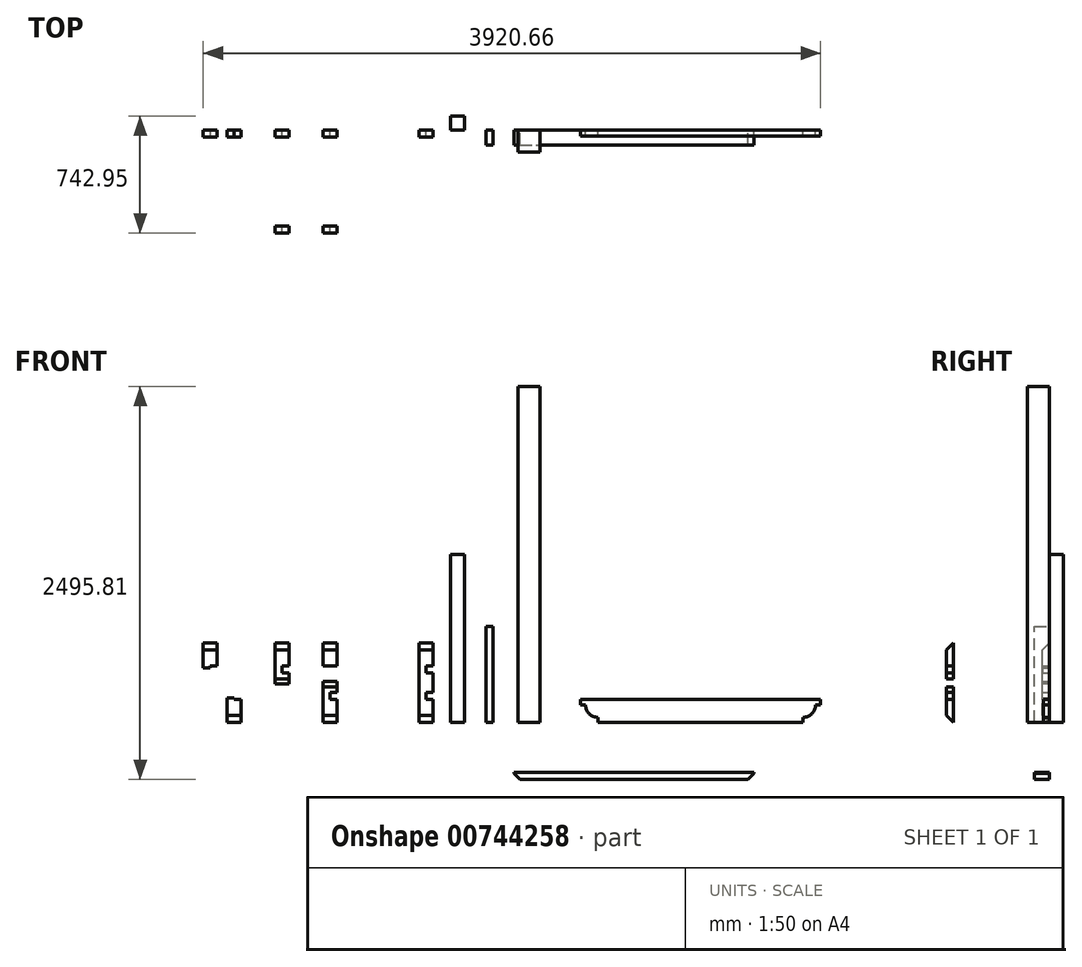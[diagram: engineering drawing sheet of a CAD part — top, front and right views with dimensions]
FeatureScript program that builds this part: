
annotation { "Feature Type Name" : "Feature", "Feature Type Description" : "" }
export const myFeature = defineFeature(function(context is Context, id is Id, definition is map)
    precondition{}
    {
        {
            var Q0;
            Q0=qCreatedBy(makeId("Front.planeOp"),FACE);
            var sketch = newSketch(context, id + "F0", { "sketchPlane" : qUnion([Q0])});
            skLineSegment(sketch, "E0.bottom", {"start": v(25.4, 0) * mm, "end": v(165.1, 0) * mm});
            skLineSegment(sketch, "E0.top", {"start": v(25.4, 2133.6) * mm, "end": v(165.1, 2133.6) * mm});
            skLineSegment(sketch, "E0.left", {"start": v(25.4, 0) * mm, "end": v(25.4, 2133.6) * mm});
            skLineSegment(sketch, "E0.right", {"start": v(165.1, 0) * mm, "end": v(165.1, 2133.6) * mm});
            skSolve(sketch);
        }
        {
            var Q0;
            Q0=makeQuery(id+"F0.imprint","IMPRINT",FACE,{"disambiguationData":[TD([[makeQuery(id+"F0.imprint","IMPRINT",EDGE,{"derivedFrom":sQuery(id+"F0.wireOp",EDGE,"E0.bottom")}),1.0]])]});
            extrude(context, id + "F1", {"entities" : qUnion([Q0]), "depth" : 139.7 * mm, "offsetDistance" : 25.4 * mm});
        }
        {
            var Q0;
            Q0=qCreatedBy(makeId("Front.planeOp"),FACE);
            var sketch = newSketch(context, id + "F2", { "sketchPlane" : qUnion([Q0])});
            skLineSegment(sketch, "E1.bottom", {"start": v(534.11, 0) * mm, "end": v(1835.86, 0) * mm});
            skLineSegment(sketch, "E1.top", {"start": v(422.99, 146.05) * mm, "end": v(1946.99, 146.05) * mm});
            skLineSegment(sketch, "E1.left", {"start": v(422.99, 111.13) * mm, "end": v(422.99, 146.05) * mm});
            skLineSegment(sketch, "E1.right", {"start": v(1946.99, 111.13) * mm, "end": v(1946.99, 146.05) * mm});
            skLineSegment(sketch, "E2", {"start": v(422.99, 111.13) * mm, "end": v(454.74, 111.13) * mm});
            skLineSegment(sketch, "E3", {"start": v(534.11, 0) * mm, "end": v(534.11, 31.75) * mm});
            skArc(sketch, "E4", {"start": v(454.74, 111.13) * mm, "mid": v(477.98, 55) * mm, "end": v(534.11, 31.75) * mm});
            skLineSegment(sketch, "E5", {"start": v(534.11, 31.75) * mm, "end": v(534.11, 196.01) * mm, "construction": true});
            skLineSegment(sketch, "E6", {"start": v(454.74, 111.13) * mm, "end": v(614.97, 111.13) * mm, "construction": true});
            skLineSegment(sketch, "E7", {"start": v(1946.99, 111.13) * mm, "end": v(1915.24, 111.13) * mm});
            skLineSegment(sketch, "E8", {"start": v(1835.86, 0) * mm, "end": v(1835.86, 31.75) * mm});
            skLineSegment(sketch, "E9", {"start": v(1835.86, 31.75) * mm, "end": v(1835.86, 138.42) * mm, "construction": true});
            skLineSegment(sketch, "E10", {"start": v(2108.59, 111.13) * mm, "end": v(1915.24, 111.13) * mm, "construction": true});
            skArc(sketch, "E11", {"start": v(1835.86, 31.75) * mm, "mid": v(1891.99, 55) * mm, "end": v(1915.24, 111.13) * mm});
            skSolve(sketch);
        }
        {
            var Q0;
            Q0=makeQuery(id+"F2.imprint","IMPRINT",FACE,{"disambiguationData":[TD([[makeQuery(id+"F2.imprint","IMPRINT",EDGE,{"derivedFrom":sQuery(id+"F2.wireOp",EDGE,"E1.bottom")}),1.0]])]});
            extrude(context, id + "F3", {"entities" : qUnion([Q0]), "depth" : 38.1 * mm, "offsetDistance" : 25.4 * mm});
        }
        {
            var Q0;
            Q0=qCreatedBy(makeId("Front.planeOp"),FACE);
            var sketch = newSketch(context, id + "F4", { "sketchPlane" : qUnion([Q0])});
            skLineSegment(sketch, "E12.bottom", {"start": v(0, -317.76) * mm, "end": v(1524, -317.76) * mm});
            skLineSegment(sketch, "E12.top", {"start": v(38.1, -362.2) * mm, "end": v(1485.9, -362.2) * mm});
            skLineSegment(sketch, "E12.left", {"start": v(0, -317.76) * mm, "end": v(0, -324.1) * mm});
            skLineSegment(sketch, "E12.right", {"start": v(1524, -317.76) * mm, "end": v(1524, -324.1) * mm});
            skLineSegment(sketch, "E13", {"start": v(0, -324.1) * mm, "end": v(38.1, -362.2) * mm});
            skLineSegment(sketch, "E14", {"start": v(1524, -324.1) * mm, "end": v(1485.9, -362.2) * mm});
            skSolve(sketch);
        }
        {
            var Q0;
            Q0=makeQuery(id+"F4.imprint","IMPRINT",FACE,{"disambiguationData":[TD([[makeQuery(id+"F4.imprint","IMPRINT",EDGE,{"derivedFrom":sQuery(id+"F4.wireOp",EDGE,"E12.bottom")}),-1.0]])]});
            extrude(context, id + "F5", {"entities" : qUnion([Q0]), "depth" : 95.25 * mm, "offsetDistance" : 25.4 * mm});
        }
        {
            var Q0;
            Q0=qCreatedBy(makeId("Top.planeOp"),FACE);
            var sketch = newSketch(context, id + "F6", { "sketchPlane" : qUnion([Q0])});
            skLineSegment(sketch, "E15.bottom", {"start": v(-313.33, 0) * mm, "end": v(-402.23, 0) * mm});
            skLineSegment(sketch, "E15.top", {"start": v(-313.33, 88.9) * mm, "end": v(-402.23, 88.9) * mm});
            skLineSegment(sketch, "E15.left", {"start": v(-313.33, 0) * mm, "end": v(-313.33, 88.9) * mm});
            skLineSegment(sketch, "E15.right", {"start": v(-402.23, 0) * mm, "end": v(-402.23, 88.9) * mm});
            skSolve(sketch);
        }
        {
            var Q0;
            Q0=makeQuery(id+"F6.imprint","IMPRINT",FACE,{"disambiguationData":[TD([[makeQuery(id+"F6.imprint","IMPRINT",EDGE,{"derivedFrom":sQuery(id+"F6.wireOp",EDGE,"E15.bottom")}),-1.0]])]});
            extrude(context, id + "F7", {"entities" : qUnion([Q0]), "depth" : 1066.8 * mm, "offsetDistance" : 25.4 * mm});
        }
        {
            var Q0;
            Q0=qCreatedBy(makeId("Front.planeOp"),FACE);
            var sketch = newSketch(context, id + "F8", { "sketchPlane" : qUnion([Q0])});
            skLineSegment(sketch, "E16.bottom", {"start": v(-133.21, 0) * mm, "end": v(-177.66, 0) * mm});
            skLineSegment(sketch, "E16.top", {"start": v(-133.21, 609.6) * mm, "end": v(-177.66, 609.6) * mm});
            skLineSegment(sketch, "E16.left", {"start": v(-133.21, 0) * mm, "end": v(-133.21, 609.6) * mm});
            skLineSegment(sketch, "E16.right", {"start": v(-177.66, 0) * mm, "end": v(-177.66, 609.6) * mm});
            skSolve(sketch);
        }
        {
            var Q0;
            Q0=makeQuery(id+"F8.imprint","IMPRINT",FACE,{"disambiguationData":[TD([[makeQuery(id+"F8.imprint","IMPRINT",EDGE,{"derivedFrom":sQuery(id+"F8.wireOp",EDGE,"E16.bottom")}),-1.0]])]});
            extrude(context, id + "F9", {"entities" : qUnion([Q0]), "depth" : 95.25 * mm, "offsetDistance" : 25.4 * mm});
        }
        {
            var Q0;
            Q0=qCreatedBy(makeId("Front.planeOp"),FACE);
            var sketch = newSketch(context, id + "F10", { "sketchPlane" : qUnion([Q0])});
            skLineSegment(sketch, "E17", {"start": v(-602.07, 0) * mm, "end": v(-602.07, 504.83) * mm});
            skLineSegment(sketch, "E18", {"start": v(-602.07, 0) * mm, "end": v(-513.17, 0) * mm});
            skLineSegment(sketch, "E19", {"start": v(-602.07, 504.83) * mm, "end": v(-513.17, 504.83) * mm});
            skLineSegment(sketch, "E20", {"start": v(-513.17, 0) * mm, "end": v(-513.17, 146.05) * mm});
            skLineSegment(sketch, "E21", {"start": v(-602.07, 336.55) * mm, "end": v(-513.17, 336.55) * mm, "construction": true});
            skLineSegment(sketch, "E22", {"start": v(-602.07, 168.28) * mm, "end": v(-513.17, 168.28) * mm, "construction": true});
            skLineSegment(sketch, "E23.bottom", {"start": v(-513.17, 146.05) * mm, "end": v(-557.62, 146.05) * mm});
            skLineSegment(sketch, "E23.top", {"start": v(-513.17, 190.5) * mm, "end": v(-557.62, 190.5) * mm});
            skLineSegment(sketch, "E23.right", {"start": v(-557.62, 146.05) * mm, "end": v(-557.62, 190.5) * mm});
            skLineSegment(sketch, "E24.bottom", {"start": v(-513.17, 358.78) * mm, "end": v(-557.62, 358.78) * mm});
            skLineSegment(sketch, "E24.top", {"start": v(-513.17, 314.33) * mm, "end": v(-557.62, 314.33) * mm});
            skLineSegment(sketch, "E24.right", {"start": v(-557.62, 358.78) * mm, "end": v(-557.62, 314.33) * mm});
            skLineSegment(sketch, "E25.trimOffspring", {"start": v(-513.17, 358.78) * mm, "end": v(-513.17, 504.83) * mm});
            skLineSegment(sketch, "E26.trimOffspring", {"start": v(-513.17, 190.5) * mm, "end": v(-513.17, 314.33) * mm});
            skSolve(sketch);
        }
        {
            var Q0;
            Q0=makeQuery(id+"F10.imprint","IMPRINT",FACE,{"disambiguationData":[TD([[makeQuery(id+"F10.imprint","IMPRINT",EDGE,{"derivedFrom":sQuery(id+"F10.wireOp",EDGE,"E17")}),-1.0]])]});
            extrude(context, id + "F11", {"entities" : qUnion([Q0]), "depth" : 44.45 * mm, "offsetDistance" : 25.4 * mm});
        }
        {
            var Q0;
            Q0=makeQuery(id+"F11.opExtrude","SWEPT_FACE",FACE,{"disambiguationData":[OSD([sQuery(id+"F10.wireOp",EDGE,"E17")])]});
            var sketch = newSketch(context, id + "F12", { "sketchPlane" : qUnion([Q0])});
            skLineSegment(sketch, "E27", {"start": v(0, 0) * mm, "end": v(44.45, 44.45) * mm});
            skLineSegment(sketch, "E28", {"start": v(44.45, 44.45) * mm, "end": v(44.45, 0) * mm});
            skLineSegment(sketch, "E29", {"start": v(44.45, 0) * mm, "end": v(0, 0) * mm});
            skLineSegment(sketch, "E30", {"start": v(0, 504.83) * mm, "end": v(44.45, 460.38) * mm});
            skLineSegment(sketch, "E31", {"start": v(0, 504.83) * mm, "end": v(44.45, 504.83) * mm});
            skLineSegment(sketch, "E32", {"start": v(44.45, 504.83) * mm, "end": v(44.45, 460.38) * mm});
            skSolve(sketch);
        }
        {
            var Q0;
            Q0=makeQuery(id+"F12.imprint","IMPRINT",FACE,{"disambiguationData":[TD([[makeQuery(id+"F12.imprint","IMPRINT",EDGE,{"derivedFrom":sQuery(id+"F12.wireOp",EDGE,"E30")}),1.0]])]});
            var Q1;
            Q1=makeQuery(id+"F12.imprint","IMPRINT",FACE,{"disambiguationData":[TD([[makeQuery(id+"F12.imprint","IMPRINT",EDGE,{"derivedFrom":sQuery(id+"F12.wireOp",EDGE,"E27")}),-1.0]])]});
            extrude(context, id + "F13", {"entities" : qUnion([Q0, Q1]), "operationType" : NewBodyOperationType.REMOVE, "oppositeDirection" : true, "depth" : 88.9 * mm, "offsetDistance" : 25.4 * mm});
        }
        {
            var Q0;
            Q0=makeQuery(id+"F11.opExtrude","SWEPT_BODY",BODY,{"disambiguationData":[OSD([sQuery(id+"F10.wireOp",EDGE,"E17"),sQuery(id+"F10.wireOp",EDGE,"E18"),sQuery(id+"F10.wireOp",EDGE,"E19"),sQuery(id+"F10.wireOp",EDGE,"E20"),sQuery(id+"F10.wireOp",EDGE,"E23.bottom"),sQuery(id+"F10.wireOp",EDGE,"E23.top"),sQuery(id+"F10.wireOp",EDGE,"E23.right"),sQuery(id+"F10.wireOp",EDGE,"E24.bottom"),sQuery(id+"F10.wireOp",EDGE,"E24.top"),sQuery(id+"F10.wireOp",EDGE,"E24.right"),sQuery(id+"F10.wireOp",EDGE,"E25.trimOffspring"),sQuery(id+"F10.wireOp",EDGE,"E26.trimOffspring")])]});
            transform(context, id + "F14", {"entities" : qUnion([Q0]), "transformType" : TransformType.TRANSLATION_3D, "dx" : -609.6 * mm, "dy" : 0 * mm, "dz" : 0 * mm, "makeCopy" : true});
        }
        {
            var Q0;
            Q0=makeQuery(id+"F14.opPattern","COPY",FACE,{"derivedFrom":makeQuery(id+"F11.opExtrude","SWEPT_FACE",FACE,{"disambiguationData":[OSD([sQuery(id+"F10.wireOp",EDGE,"E25.trimOffspring")])]}),"instanceName":"1"});
            var sketch = newSketch(context, id + "F15", { "sketchPlane" : qUnion([Q0])});
            skLineSegment(sketch, "E33.bottom", {"start": v(0, 260.35) * mm, "end": v(-45.72, 260.35) * mm});
            skLineSegment(sketch, "E33.top", {"start": v(0, 768.35) * mm, "end": v(-45.72, 768.35) * mm});
            skLineSegment(sketch, "E33.left", {"start": v(0, 260.35) * mm, "end": v(0, 768.35) * mm});
            skLineSegment(sketch, "E33.right", {"start": v(-45.72, 260.35) * mm, "end": v(-45.72, 768.35) * mm});
            skSolve(sketch);
        }
        {
            var Q0;
            {var subQ5=sQuery(id+"F15.wireOp",EDGE,"E33.bottom");Q0=makeQuery(id+"F15.imprint","IMPRINT",FACE,{"disambiguationData":[TD([[makeQuery(id+"F15.imprint","IMPRINT",EDGE,{"derivedFrom":subQ5}),-1.0]])]});}
            var Q1;
            {var subQ3=makeQuery(id+"F14.opPattern","COPY",EDGE,{"derivedFrom":makeQuery(id+"F13.boolean.opBoolean","COPY",EDGE,{"derivedFrom":makeQuery(id+"F13.opExtrude","CAP_EDGE",EDGE,{"disambiguationData":[OSD([sQuery(id+"F12.wireOp",EDGE,"E30")])],"isStart":false})}),"instanceName":"1"});Q1=makeQuery(id+"F15.imprint","IMPRINT",FACE,{"disambiguationData":[TD([[makeQuery(id+"F15.imprint","IMPRINT",EDGE,{"derivedFrom":subQ3}),1.0]])]});}
            extrude(context, id + "F16", {"entities" : qUnion([Q0, Q1]), "operationType" : NewBodyOperationType.REMOVE, "oppositeDirection" : true, "depth" : 101.6 * mm, "offsetDistance" : 25.4 * mm});
        }
        {
            var Q0;
            Q0=makeQuery(id+"F11.opExtrude","SWEPT_BODY",BODY,{"disambiguationData":[OSD([sQuery(id+"F10.wireOp",EDGE,"E17"),sQuery(id+"F10.wireOp",EDGE,"E18"),sQuery(id+"F10.wireOp",EDGE,"E19"),sQuery(id+"F10.wireOp",EDGE,"E20"),sQuery(id+"F10.wireOp",EDGE,"E23.bottom"),sQuery(id+"F10.wireOp",EDGE,"E23.top"),sQuery(id+"F10.wireOp",EDGE,"E23.right"),sQuery(id+"F10.wireOp",EDGE,"E24.bottom"),sQuery(id+"F10.wireOp",EDGE,"E24.top"),sQuery(id+"F10.wireOp",EDGE,"E24.right"),sQuery(id+"F10.wireOp",EDGE,"E25.trimOffspring"),sQuery(id+"F10.wireOp",EDGE,"E26.trimOffspring")])]});
            transform(context, id + "F17", {"entities" : qUnion([Q0]), "transformType" : TransformType.TRANSLATION_3D, "dx" : -914.4 * mm, "dy" : 0 * mm, "dz" : 0 * mm, "makeCopy" : true});
        }
        {
            var Q0;
            Q0=makeQuery(id+"F17.opPattern","COPY",FACE,{"derivedFrom":makeQuery(id+"F11.opExtrude","SWEPT_FACE",FACE,{"disambiguationData":[OSD([sQuery(id+"F10.wireOp",EDGE,"E26.trimOffspring")])]}),"instanceName":"1"});
            var sketch = newSketch(context, id + "F18", { "sketchPlane" : qUnion([Q0])});
            skLineSegment(sketch, "E34.bottom", {"start": v(-44.45, 244.47) * mm, "end": v(0, 244.47) * mm});
            skLineSegment(sketch, "E34.top", {"start": v(-44.45, -52.06) * mm, "end": v(0, -52.06) * mm});
            skLineSegment(sketch, "E34.left", {"start": v(-44.45, 244.47) * mm, "end": v(-44.45, -52.06) * mm});
            skLineSegment(sketch, "E34.right", {"start": v(0, 244.47) * mm, "end": v(0, -52.06) * mm});
            skSolve(sketch);
        }
        {
            var Q0;
            {var subQ0=sQuery(id+"F18.wireOp",EDGE,"E34.top");Q0=makeQuery(id+"F18.imprint","IMPRINT",FACE,{"disambiguationData":[TD([[makeQuery(id+"F18.imprint","IMPRINT",EDGE,{"derivedFrom":subQ0}),1.0]])]});}
            var Q1;
            {var subQ0=sQuery(id+"F18.wireOp",EDGE,"E34.bottom");Q1=makeQuery(id+"F18.imprint","IMPRINT",FACE,{"disambiguationData":[TD([[makeQuery(id+"F18.imprint","IMPRINT",EDGE,{"derivedFrom":subQ0}),-1.0]])]});}
            extrude(context, id + "F19", {"entities" : qUnion([Q0, Q1]), "operationType" : NewBodyOperationType.REMOVE, "oppositeDirection" : true, "depth" : 101.6 * mm, "offsetDistance" : 25.4 * mm});
        }
        {
            var Q0;
            Q0=makeQuery(id+"F11.opExtrude","SWEPT_BODY",BODY,{"disambiguationData":[OSD([sQuery(id+"F10.wireOp",EDGE,"E17"),sQuery(id+"F10.wireOp",EDGE,"E18"),sQuery(id+"F10.wireOp",EDGE,"E19"),sQuery(id+"F10.wireOp",EDGE,"E20"),sQuery(id+"F10.wireOp",EDGE,"E23.bottom"),sQuery(id+"F10.wireOp",EDGE,"E23.top"),sQuery(id+"F10.wireOp",EDGE,"E23.right"),sQuery(id+"F10.wireOp",EDGE,"E24.bottom"),sQuery(id+"F10.wireOp",EDGE,"E24.top"),sQuery(id+"F10.wireOp",EDGE,"E24.right"),sQuery(id+"F10.wireOp",EDGE,"E25.trimOffspring"),sQuery(id+"F10.wireOp",EDGE,"E26.trimOffspring")])]});
            transform(context, id + "F20", {"entities" : qUnion([Q0]), "transformType" : TransformType.TRANSLATION_3D, "dx" : -1219.2 * mm, "dy" : 0 * mm, "dz" : 0 * mm, "makeCopy" : true});
        }
        {
            var Q0;
            Q0=makeQuery(id+"F20.opPattern","COPY",FACE,{"derivedFrom":makeQuery(id+"F11.opExtrude","SWEPT_FACE",FACE,{"disambiguationData":[OSD([sQuery(id+"F10.wireOp",EDGE,"E26.trimOffspring")])]}),"instanceName":"1"});
            var sketch = newSketch(context, id + "F21", { "sketchPlane" : qUnion([Q0])});
            skLineSegment(sketch, "E35.bottom", {"start": v(0, 504.83) * mm, "end": v(-44.45, 504.83) * mm});
            skLineSegment(sketch, "E35.top", {"start": v(0, 157.18) * mm, "end": v(-44.45, 157.18) * mm});
            skLineSegment(sketch, "E35.left", {"start": v(0, 504.83) * mm, "end": v(0, 157.18) * mm});
            skLineSegment(sketch, "E35.right", {"start": v(-44.45, 504.83) * mm, "end": v(-44.45, 157.18) * mm});
            skSolve(sketch);
        }
        {
            var Q0;
            {var subQ0=sQuery(id+"F21.wireOp",EDGE,"E35.top");Q0=makeQuery(id+"F21.imprint","IMPRINT",FACE,{"disambiguationData":[TD([[makeQuery(id+"F21.imprint","IMPRINT",EDGE,{"derivedFrom":subQ0}),-1.0]])]});}
            var Q1;
            {var subQ1=sQuery(id+"F10.wireOp",EDGE,"E26.trimOffspring");var subQ2=makeQuery(id+"F20.opPattern","COPY",EDGE,{"derivedFrom":makeQuery(id+"F11.opExtrude","SWEPT_EDGE",EDGE,{"disambiguationData":[OSD([sQuery(id+"F10.wireOp",EDGE,"E23.top"),subQ1])]}),"instanceName":"1"});Q1=makeQuery(id+"F21.imprint","IMPRINT",FACE,{"disambiguationData":[TD([[makeQuery(id+"F21.imprint","IMPRINT",EDGE,{"derivedFrom":subQ2}),1.0]])]});}
            var Q2;
            {var subQ0=sQuery(id+"F21.wireOp",EDGE,"E35.bottom");Q2=makeQuery(id+"F21.imprint","IMPRINT",FACE,{"disambiguationData":[TD([[makeQuery(id+"F21.imprint","IMPRINT",EDGE,{"derivedFrom":subQ0}),1.0]])]});}
            extrude(context, id + "F22", {"entities" : qUnion([Q0, Q1, Q2]), "operationType" : NewBodyOperationType.REMOVE, "oppositeDirection" : true, "depth" : 101.6 * mm, "offsetDistance" : 25.4 * mm});
        }
        {
            var Q0;
            Q0=makeQuery(id+"F11.opExtrude","SWEPT_BODY",BODY,{"disambiguationData":[OSD([sQuery(id+"F10.wireOp",EDGE,"E17"),sQuery(id+"F10.wireOp",EDGE,"E18"),sQuery(id+"F10.wireOp",EDGE,"E19"),sQuery(id+"F10.wireOp",EDGE,"E20"),sQuery(id+"F10.wireOp",EDGE,"E23.bottom"),sQuery(id+"F10.wireOp",EDGE,"E23.top"),sQuery(id+"F10.wireOp",EDGE,"E23.right"),sQuery(id+"F10.wireOp",EDGE,"E24.bottom"),sQuery(id+"F10.wireOp",EDGE,"E24.top"),sQuery(id+"F10.wireOp",EDGE,"E24.right"),sQuery(id+"F10.wireOp",EDGE,"E25.trimOffspring"),sQuery(id+"F10.wireOp",EDGE,"E26.trimOffspring")])]});
            transform(context, id + "F23", {"entities" : qUnion([Q0]), "transformType" : TransformType.TRANSLATION_3D, "dx" : -1371.6 * mm, "dy" : 0 * mm, "dz" : 0 * mm, "makeCopy" : true});
        }
        {
            var Q0;
            Q0=makeQuery(id+"F23.opPattern","COPY",FACE,{"derivedFrom":makeQuery(id+"F11.opExtrude","SWEPT_FACE",FACE,{"disambiguationData":[OSD([sQuery(id+"F10.wireOp",EDGE,"E26.trimOffspring")])]}),"instanceName":"1"});
            var sketch = newSketch(context, id + "F24", { "sketchPlane" : qUnion([Q0])});
            skLineSegment(sketch, "E36.bottom", {"start": v(0, 0) * mm, "end": v(-51.19, 0) * mm});
            skLineSegment(sketch, "E36.top", {"start": v(0, 347.65) * mm, "end": v(-51.19, 347.65) * mm});
            skLineSegment(sketch, "E36.left", {"start": v(0, 0) * mm, "end": v(0, 347.65) * mm});
            skLineSegment(sketch, "E36.right", {"start": v(-51.19, 0) * mm, "end": v(-51.19, 347.65) * mm});
            skSolve(sketch);
        }
        {
            var Q0;
            {var subQ1=sQuery(id+"F10.wireOp",EDGE,"E26.trimOffspring");Q0=makeQuery(id+"F24.imprint","IMPRINT",FACE,{"disambiguationData":[TD([[makeQuery(id+"F24.imprint","IMPRINT",EDGE,{"derivedFrom":makeQuery(id+"F23.opPattern","COPY",EDGE,{"derivedFrom":makeQuery(id+"F11.opExtrude","CAP_EDGE",EDGE,{"disambiguationData":[OSD([subQ1])],"isStart":false}),"instanceName":"1"})}),-1.0]])]});}
            var Q1;
            {var subQ5=sQuery(id+"F24.wireOp",EDGE,"E36.bottom");Q1=makeQuery(id+"F24.imprint","IMPRINT",FACE,{"disambiguationData":[TD([[makeQuery(id+"F24.imprint","IMPRINT",EDGE,{"derivedFrom":subQ5}),-1.0]])]});}
            extrude(context, id + "F25", {"entities" : qUnion([Q0, Q1]), "operationType" : NewBodyOperationType.REMOVE, "oppositeDirection" : true, "depth" : 101.6 * mm, "offsetDistance" : 25.4 * mm});
        }
        {
            var Q0;
            Q0=makeQuery(id+"F11.opExtrude","SWEPT_BODY",BODY,{"disambiguationData":[OSD([sQuery(id+"F10.wireOp",EDGE,"E17"),sQuery(id+"F10.wireOp",EDGE,"E18"),sQuery(id+"F10.wireOp",EDGE,"E19"),sQuery(id+"F10.wireOp",EDGE,"E20"),sQuery(id+"F10.wireOp",EDGE,"E23.bottom"),sQuery(id+"F10.wireOp",EDGE,"E23.top"),sQuery(id+"F10.wireOp",EDGE,"E23.right"),sQuery(id+"F10.wireOp",EDGE,"E24.bottom"),sQuery(id+"F10.wireOp",EDGE,"E24.top"),sQuery(id+"F10.wireOp",EDGE,"E24.right"),sQuery(id+"F10.wireOp",EDGE,"E25.trimOffspring"),sQuery(id+"F10.wireOp",EDGE,"E26.trimOffspring")])]});
            transform(context, id + "F26", {"entities" : qUnion([Q0]), "transformType" : TransformType.TRANSLATION_3D, "dx" : -609.6 * mm, "dy" : -609.6 * mm, "dz" : 0 * mm, "makeCopy" : true});
        }
        {
            var Q0;
            Q0=makeQuery(id+"F26.opPattern","COPY",FACE,{"derivedFrom":makeQuery(id+"F11.opExtrude","SWEPT_FACE",FACE,{"disambiguationData":[OSD([sQuery(id+"F10.wireOp",EDGE,"E26.trimOffspring")])]}),"instanceName":"1"});
            var sketch = newSketch(context, id + "F27", { "sketchPlane" : qUnion([Q0])});
            skLineSegment(sketch, "E37.bottom", {"start": v(-609.6, 507.13) * mm, "end": v(-654.05, 507.13) * mm});
            skLineSegment(sketch, "E37.top", {"start": v(-609.6, 227) * mm, "end": v(-654.05, 227) * mm});
            skLineSegment(sketch, "E37.left", {"start": v(-609.6, 507.13) * mm, "end": v(-609.6, 227) * mm});
            skLineSegment(sketch, "E37.right", {"start": v(-654.05, 507.13) * mm, "end": v(-654.05, 227) * mm});
            skSolve(sketch);
        }
        {
            var Q0;
            {var subQ0=sQuery(id+"F27.wireOp",EDGE,"E37.top");Q0=makeQuery(id+"F27.imprint","IMPRINT",FACE,{"disambiguationData":[TD([[makeQuery(id+"F27.imprint","IMPRINT",EDGE,{"derivedFrom":subQ0}),-1.0]])]});}
            var Q1;
            {var subQ0=sQuery(id+"F27.wireOp",EDGE,"E37.bottom");Q1=makeQuery(id+"F27.imprint","IMPRINT",FACE,{"disambiguationData":[TD([[makeQuery(id+"F27.imprint","IMPRINT",EDGE,{"derivedFrom":subQ0}),1.0]])]});}
            extrude(context, id + "F28", {"entities" : qUnion([Q0, Q1]), "operationType" : NewBodyOperationType.REMOVE, "oppositeDirection" : true, "depth" : 101.6 * mm, "offsetDistance" : 25.4 * mm});
        }
        {
            var Q0;
            Q0=makeQuery(id+"F11.opExtrude","SWEPT_BODY",BODY,{"disambiguationData":[OSD([sQuery(id+"F10.wireOp",EDGE,"E17"),sQuery(id+"F10.wireOp",EDGE,"E18"),sQuery(id+"F10.wireOp",EDGE,"E19"),sQuery(id+"F10.wireOp",EDGE,"E20"),sQuery(id+"F10.wireOp",EDGE,"E23.bottom"),sQuery(id+"F10.wireOp",EDGE,"E23.top"),sQuery(id+"F10.wireOp",EDGE,"E23.right"),sQuery(id+"F10.wireOp",EDGE,"E24.bottom"),sQuery(id+"F10.wireOp",EDGE,"E24.top"),sQuery(id+"F10.wireOp",EDGE,"E24.right"),sQuery(id+"F10.wireOp",EDGE,"E25.trimOffspring"),sQuery(id+"F10.wireOp",EDGE,"E26.trimOffspring")])]});
            transform(context, id + "F29", {"entities" : qUnion([Q0]), "transformType" : TransformType.TRANSLATION_3D, "dx" : -914.4 * mm, "dy" : -609.6 * mm, "dz" : 0 * mm, "makeCopy" : true});
        }
        {
            var Q0;
            Q0=makeQuery(id+"F29.opPattern","COPY",FACE,{"derivedFrom":makeQuery(id+"F11.opExtrude","SWEPT_FACE",FACE,{"disambiguationData":[OSD([sQuery(id+"F10.wireOp",EDGE,"E26.trimOffspring")])]}),"instanceName":"1"});
            var sketch = newSketch(context, id + "F30", { "sketchPlane" : qUnion([Q0])});
            skLineSegment(sketch, "E38.bottom", {"start": v(-609.57, 0) * mm, "end": v(-654.05, 0) * mm});
            skLineSegment(sketch, "E38.top", {"start": v(-609.57, 277.83) * mm, "end": v(-654.05, 277.83) * mm});
            skLineSegment(sketch, "E38.left", {"start": v(-609.57, 0) * mm, "end": v(-609.57, 277.83) * mm});
            skLineSegment(sketch, "E38.right", {"start": v(-654.05, 0) * mm, "end": v(-654.05, 277.83) * mm});
            skSolve(sketch);
        }
        {
            var Q0;
            {var subQ3=sQuery(id+"F30.wireOp",EDGE,"E38.bottom");Q0=makeQuery(id+"F30.imprint","IMPRINT",FACE,{"disambiguationData":[TD([[makeQuery(id+"F30.imprint","IMPRINT",EDGE,{"derivedFrom":subQ3}),-1.0]])]});}
            var Q1;
            {var subQ2=sQuery(id+"F10.wireOp",EDGE,"E26.trimOffspring");var subQ6=makeQuery(id+"F29.opPattern","COPY",EDGE,{"derivedFrom":makeQuery(id+"F11.opExtrude","SWEPT_EDGE",EDGE,{"disambiguationData":[OSD([sQuery(id+"F10.wireOp",EDGE,"E23.top"),subQ2])]}),"instanceName":"1"});Q1=makeQuery(id+"F30.imprint","IMPRINT",FACE,{"disambiguationData":[TD([[makeQuery(id+"F30.imprint","IMPRINT",EDGE,{"derivedFrom":subQ6}),1.0]])]});}
            extrude(context, id + "F31", {"entities" : qUnion([Q0, Q1]), "operationType" : NewBodyOperationType.REMOVE, "oppositeDirection" : true, "depth" : 101.6 * mm, "offsetDistance" : 25.4 * mm});
        }
    });
